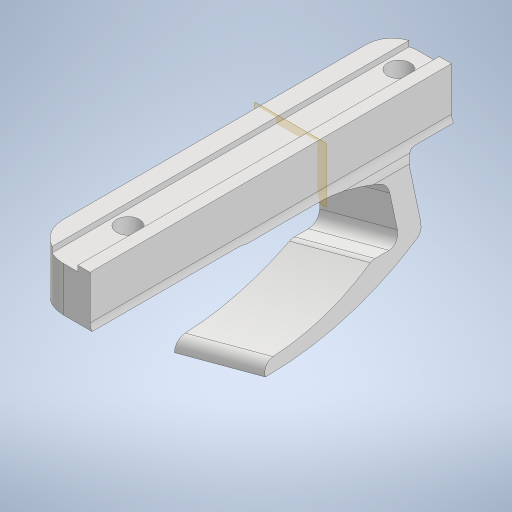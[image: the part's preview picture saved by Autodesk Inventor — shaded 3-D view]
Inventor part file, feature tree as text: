
AUTODESK INVENTOR PART (.ipt)
format: ipt  version: 2024 (Build 280153000, 153)  size: 413,696 bytes
history: native  units: mm
features: extrude x7, sketch x6, fillet x3, plane x1
ambient origin geometry x8: Origin, YZ Plane, XZ Plane, XY Plane, X Axis, Y Axis, Z Axis, Center Point
bodies: Solid1 (feature_tree)
feature tree (17):
  sketch  "Sketch1"  dims[d0=4.1mm d1=3.2mm]
  extrude  "Extrusion1"  Depth=3.2mm
  extrude  "Extrusion2"  Depth=48.5mm
  extrude  "Extrusion3"  Depth=1.0mm
  sketch  "Sketch3"  dims[d2=7.3mm d3=48.5mm]
  plane  "Work Plane1"
  extrude  "Extrusion8"  Depth=10.0mm
  extrude  "Extrusion9"  Depth=8.0mm TaperAngle=0.0deg
  extrude  "Extrusion10"  TaperAngle=15.0deg  [1 undecoded]
  fillet  "Fillet1"  Radius=30.0mm
  fillet  "Fillet2"  Radius=11.0mm
  extrude  "Extrusion11"  Depth=2.0mm TaperAngle=0.0deg
  fillet  "Fillet3"  Radius=2.4mm
  sketch  "Sketch8"  dims[d5=3.0mm d6=1.0mm]
  sketch  "Sketch9"  dims[d7=3.2mm d8=10.0mm]
  sketch  "Sketch10"  dims[d9=1.0mm d10=0.0mm d11=8.0mm d12=0.0mm]
  sketch  "Sketch11"  dims[d13=5.0mm d14=0.0mm d30=15.0deg d31=30.0mm d32=0.0mm d33=11.0mm d34=10.9mm d35=0.0mm d36=2.4mm d37=5.0mm d38=5.0mm d39=2.0mm d40=10.9mm d41=0.0mm d42=2.0mm d43=2.0mm d44=1.0mm d45=0.0mm d46=2.0mm]
note: 1 required parameter value undecoded (feature->parameter linkage not recoverable at this tier; creation-order binding heuristic only, values carry confidence <= 0.55)
